# Revit family: Accessories-Teknion-CEASR_Recycling_Disposal_Symbol-R2023
name_source: partatom
category: Furniture
units: mm (PartAtom-declared; Revit-internal decimal feet)

## family parameters
Always vertical = Yes
Cut with Voids When Loaded = No
Enable Cutting in Views = No
OmniClass Number = 23.40.20.00
OmniClass Title = General Furniture and Specialties
Render Appearance Source = Family Geometry
Room Calculation Point = No
Shared = Yes
Work Plane-Based = No

## types (8) — shared parameters
Assembly Code = E2020200
Manufacturer = Teknion
Manufacturer Fax = 416.661.4586
Part Number = CEASR
Product Documentation Link = https://www.teknion.com
Product Line = Accessories
Product Page URL = https://www.teknion.com
Series = Expansion Casework+
Sustainability Data = https://www.teknion.com
URL = www.teknion.com
Unit Weight URL = http://www.teknion.com
Warranty = http://www.teknion.com
zero-valued in all types: Default Elevation

## per-type parameters (varying)
| type | A Cut-out | Aluminium Can | C Cut-out | D Cut-out | Description | G Cut-out | Glass | M Cut-out | Metal | Model | P Cut-out | Paper | R Cut-out | Recycling | W Cut-out | Waste |
| Aluminum Can | 0.28 " | Yes | 0.2 " | 0.2 " | Recycling/Disposal Symbol, Aluminum Can | 0.2 " | No | 0.2 " | No | CEASRA | 0.2 " | No | 0.2 " | No | 0.2 " | No |
| Compostable | 0.2 " | No | 0.28 " | 0.2 " | Recycling/Disposal Symbol, Compostable | 0.2 " | No | 0.2 " | No | CEASRC | 0.2 " | No | 0.2 " | No | 0.2 " | No |
| Refundable Containers | 0.2 " | No | 0.2 " | 0.28 " | Recycling/Disposal Symbol, Refundable Containers | 0.2 " | No | 0.2 " | No | CEASRD | 0.2 " | No | 0.2 " | No | 0.2 " | No |
| Glass | 0.2 " | No | 0.2 " | 0.2 " | Recycling/Disposal Symbol, Glass | 0.28 " | Yes | 0.2 " | No | CEASRG | 0.2 " | No | 0.2 " | No | 0.2 " | No |
| Metal | 0.2 " | No | 0.2 " | 0.2 " | Recycling/Disposal Symbol, Metal | 0.2 " | No | 0.28 " | Yes | CEASRM | 0.2 " | No | 0.2 " | No | 0.2 " | No |
| Paper | 0.2 " | No | 0.2 " | 0.2 " | Recycling/Disposal Symbol, Paper | 0.2 " | No | 0.2 " | No | CEASRP | 0.28 " | Yes | 0.2 " | No | 0.2 " | No |
| Recycling | 0.2 " | No | 0.2 " | 0.2 " | Recycling/Disposal Symbol, Recycling | 0.2 " | No | 0.2 " | No | CEASRR | 0.2 " | No | 0.28 " | Yes | 0.2 " | No |
| Waste | 0.2 " | No | 0.2 " | 0.2 " | Recycling/Disposal Symbol, Waste | 0.2 " | No | 0.2 " | No | CEASRW | 0.2 " | No | 0.2 " | No | 0.28 " | Yes |

type visibility flags (boolean, named after types; folded from table):
- Aluminum Can: Yes: (none)
- Compostable: Yes: Compostable
- Refundable Containers: Yes: Refundable Containers
- Glass: Yes: (none)
- Metal: Yes: (none)
- Paper: Yes: (none)
- Recycling: Yes: (none)
- Waste: Yes: (none)

## geometry (parser evidence)
native form markers: Sweep x2
no freeform markers — native parametric forms only
